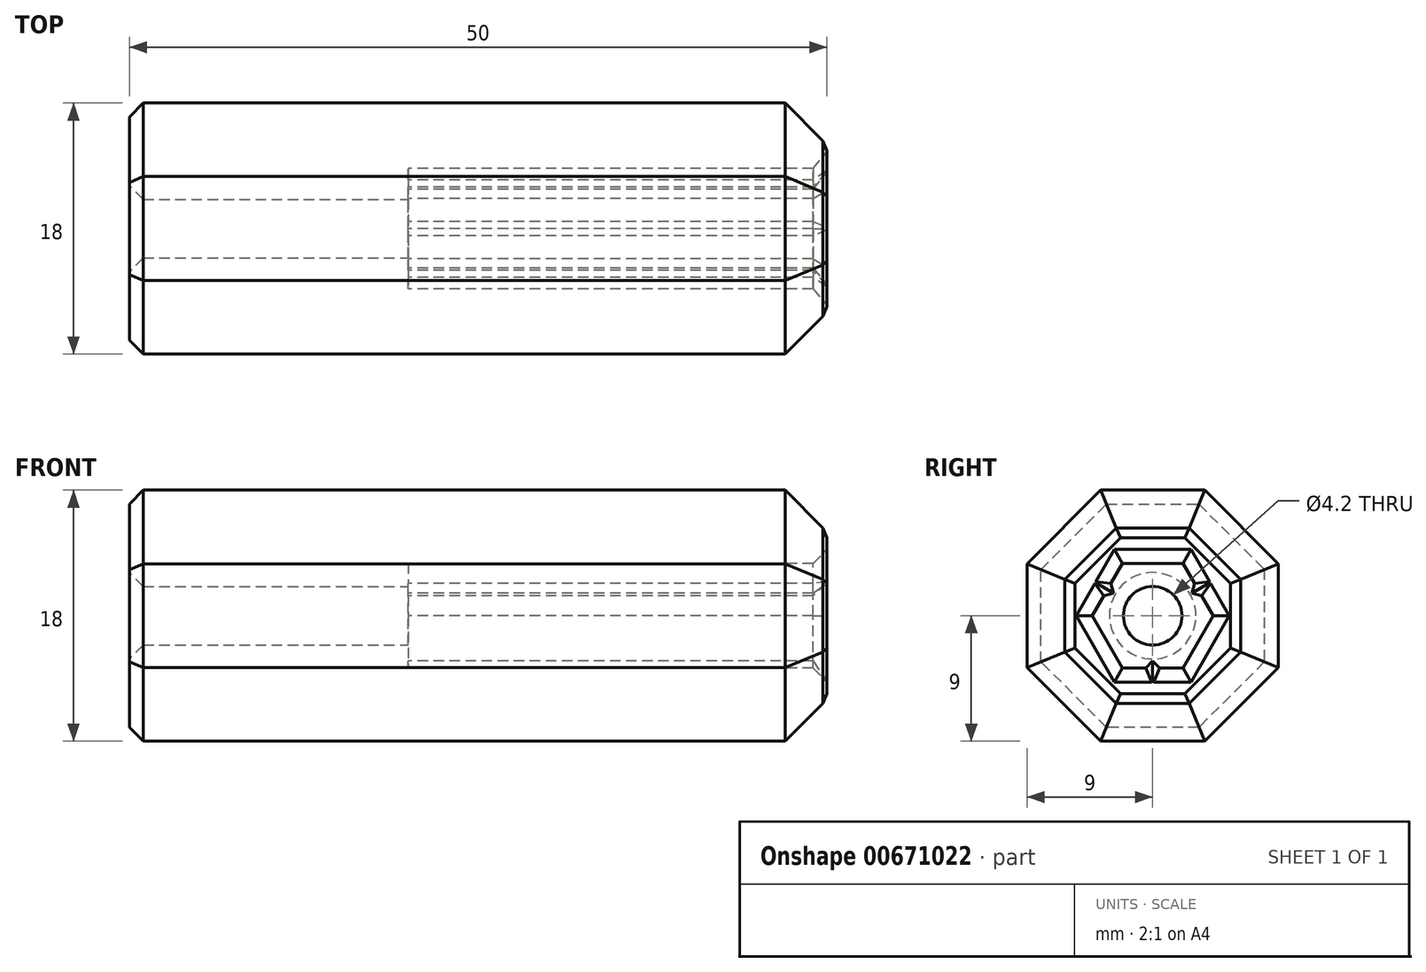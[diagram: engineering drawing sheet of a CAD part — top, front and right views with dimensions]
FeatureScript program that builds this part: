
annotation { "Feature Type Name" : "Feature", "Feature Type Description" : "" }
export const myFeature = defineFeature(function(context is Context, id is Id, definition is map)
    precondition{}
    {
        {
            var Q0;
            Q0=qCreatedBy(makeId("Right.planeOp"),FACE);
            var sketch = newSketch(context, id + "F0", { "sketchPlane" : qUnion([Q0])});
            skCircle(sketch, "E0.cCircle", {"center": v(0, 0) * mm, "radius": 9 * mm, "construction": true});
            skLineSegment(sketch, "E0.0", {"start": v(9, -3.73) * mm, "end": v(3.73, -9) * mm});
            skLineSegment(sketch, "E0.1", {"start": v(3.73, -9) * mm, "end": v(-3.73, -9) * mm});
            skLineSegment(sketch, "E0.2", {"start": v(-3.73, -9) * mm, "end": v(-9, -3.73) * mm});
            skLineSegment(sketch, "E0.3", {"start": v(-9, -3.73) * mm, "end": v(-9, 3.73) * mm});
            skLineSegment(sketch, "E0.4", {"start": v(-9, 3.73) * mm, "end": v(-3.73, 9) * mm});
            skLineSegment(sketch, "E0.5", {"start": v(-3.73, 9) * mm, "end": v(3.73, 9) * mm});
            skLineSegment(sketch, "E0.6", {"start": v(3.73, 9) * mm, "end": v(9, 3.73) * mm});
            skLineSegment(sketch, "E0.7", {"start": v(9, 3.73) * mm, "end": v(9, -3.73) * mm});
            skPoint(sketch, "E0.0.midPoint", {"position": v(6.36, -6.36) * mm});
            skSolve(sketch);
        }
        {
            var Q0;
            Q0 = qSketchRegion(id + "F0", true);
            extrude(context, id + "F1", {"entities" : qUnion([Q0]), "depth" : 50 * mm, "offsetDistance" : 25 * mm});
        }
        {
            var Q0;
            Q0=qCreatedBy(makeId("Right.planeOp"),FACE);
            cPlane(context, id + "F2", {"entities" : qUnion([Q0]), "cplaneType" : CPlaneType.OFFSET, "offset" : 20 * mm, "width" : 150 * mm, "height" : 150 * mm});
        }
        {
            var Q0;
            Q0=makeQuery(id+"F1.opExtrude","CAP_FACE",FACE,{"disambiguationData":[OSD([sQuery(id+"F0.wireOp",EDGE,"E0.0"),sQuery(id+"F0.wireOp",EDGE,"E0.1"),sQuery(id+"F0.wireOp",EDGE,"E0.2"),sQuery(id+"F0.wireOp",EDGE,"E0.3"),sQuery(id+"F0.wireOp",EDGE,"E0.4"),sQuery(id+"F0.wireOp",EDGE,"E0.5"),sQuery(id+"F0.wireOp",EDGE,"E0.6"),sQuery(id+"F0.wireOp",EDGE,"E0.7")])],"isStart":false});
            chamfer(context, id + "F3", {"entities" : qUnion([Q0]), "width" : 3 * mm, "tangentPropagation" : true});
        }
        {
            var Q0;
            Q0=qCreatedBy(id+"F2.planeOp",FACE);
            var sketch = newSketch(context, id + "F4", { "sketchPlane" : qUnion([Q0])});
            skCircle(sketch, "E1", {"center": v(0, 0) * mm, "radius": 2.1 * mm});
            skCircle(sketch, "E2.cCircle", {"center": v(0, 0) * mm, "radius": 3.75 * mm, "construction": true});
            skLineSegment(sketch, "E2.0", {"start": v(4.33, 0) * mm, "end": v(2.17, -3.75) * mm});
            skLineSegment(sketch, "E2.1", {"start": v(2.17, -3.75) * mm, "end": v(0.5, -3.75) * mm});
            skLineSegment(sketch, "E2.2", {"start": v(-2.17, -3.75) * mm, "end": v(-4.33, 0) * mm});
            skLineSegment(sketch, "E2.4", {"start": v(-2.17, 3.75) * mm, "end": v(2.17, 3.75) * mm});
            skPoint(sketch, "E2.0.midPoint", {"position": v(3.25, -1.87) * mm});
            skLineSegment(sketch, "E3", {"start": v(-0.5, -3.75) * mm, "end": v(0, -3.25) * mm});
            skLineSegment(sketch, "E4", {"start": v(0, -3.25) * mm, "end": v(0.5, -3.75) * mm});
            skLineSegment(sketch, "E5.trimOffspring", {"start": v(-0.5, -3.75) * mm, "end": v(-2.17, -3.75) * mm});
            skLineSegment(sketch, "E6.1.0", {"start": v(3.5, 1.44) * mm, "end": v(4.33, 0) * mm});
            skLineSegment(sketch, "E6.1.1", {"start": v(3.5, 1.44) * mm, "end": v(2.81, 1.62) * mm});
            skLineSegment(sketch, "E6.1.2", {"start": v(2.81, 1.62) * mm, "end": v(3, 2.3) * mm});
            skLineSegment(sketch, "E6.1.3", {"start": v(2.17, 3.75) * mm, "end": v(3, 2.3) * mm});
            skLineSegment(sketch, "E6.2.0", {"start": v(-3, 2.3) * mm, "end": v(-2.17, 3.75) * mm});
            skLineSegment(sketch, "E6.2.1", {"start": v(-3, 2.3) * mm, "end": v(-2.81, 1.62) * mm});
            skLineSegment(sketch, "E6.2.2", {"start": v(-2.81, 1.62) * mm, "end": v(-3.5, 1.44) * mm});
            skLineSegment(sketch, "E6.2.3", {"start": v(-4.33, 0) * mm, "end": v(-3.5, 1.44) * mm});
            skSolve(sketch);
        }
        {
            var Q0;
            Q0=makeQuery(id+"F4.imprint","IMPRINT",FACE,{"disambiguationData":[TD([[makeQuery(id+"F4.imprint","IMPRINT",EDGE,{"derivedFrom":sQuery(id+"F4.wireOp",EDGE,"E1")}),1.0]])]});
            extrude(context, id + "F5", {"entities" : qUnion([Q0]), "operationType" : NewBodyOperationType.REMOVE, "endBound" : BoundingType.THROUGH_ALL, "oppositeDirection" : true, "depth" : 25 * mm, "offsetDistance" : 25 * mm});
        }
        {
            var Q0;
            Q0=makeQuery(id+"F4.imprint","IMPRINT",FACE,{"disambiguationData":[TD([[makeQuery(id+"F4.imprint","IMPRINT",EDGE,{"derivedFrom":sQuery(id+"F4.wireOp",EDGE,"E1")}),1.0]])]});
            var Q1;
            Q1=makeQuery(id+"F4.imprint","IMPRINT",FACE,{"disambiguationData":[TD([[makeQuery(id+"F4.imprint","IMPRINT",EDGE,{"derivedFrom":sQuery(id+"F4.wireOp",EDGE,"E1")}),-1.0]])]});
            extrude(context, id + "F6", {"entities" : qUnion([Q0, Q1]), "operationType" : NewBodyOperationType.REMOVE, "endBound" : BoundingType.THROUGH_ALL, "depth" : 25 * mm, "offsetDistance" : 25 * mm});
        }
        {
            var Q0;
            Q0=makeQuery(id+"F1.opExtrude","CAP_FACE",FACE,{"disambiguationData":[OSD([sQuery(id+"F0.wireOp",EDGE,"E0.0"),sQuery(id+"F0.wireOp",EDGE,"E0.1"),sQuery(id+"F0.wireOp",EDGE,"E0.2"),sQuery(id+"F0.wireOp",EDGE,"E0.3"),sQuery(id+"F0.wireOp",EDGE,"E0.4"),sQuery(id+"F0.wireOp",EDGE,"E0.5"),sQuery(id+"F0.wireOp",EDGE,"E0.6"),sQuery(id+"F0.wireOp",EDGE,"E0.7")])],"isStart":true});
            var Q1;
            Q1=makeQuery(id+"F1.opExtrude","CAP_FACE",FACE,{"disambiguationData":[OSD([sQuery(id+"F0.wireOp",EDGE,"E0.0"),sQuery(id+"F0.wireOp",EDGE,"E0.1"),sQuery(id+"F0.wireOp",EDGE,"E0.2"),sQuery(id+"F0.wireOp",EDGE,"E0.3"),sQuery(id+"F0.wireOp",EDGE,"E0.4"),sQuery(id+"F0.wireOp",EDGE,"E0.5"),sQuery(id+"F0.wireOp",EDGE,"E0.6"),sQuery(id+"F0.wireOp",EDGE,"E0.7")])],"isStart":false});
            chamfer(context, id + "F7", {"entities" : qUnion([Q0, Q1]), "width" : 1 * mm, "tangentPropagation" : true});
        }
    });
